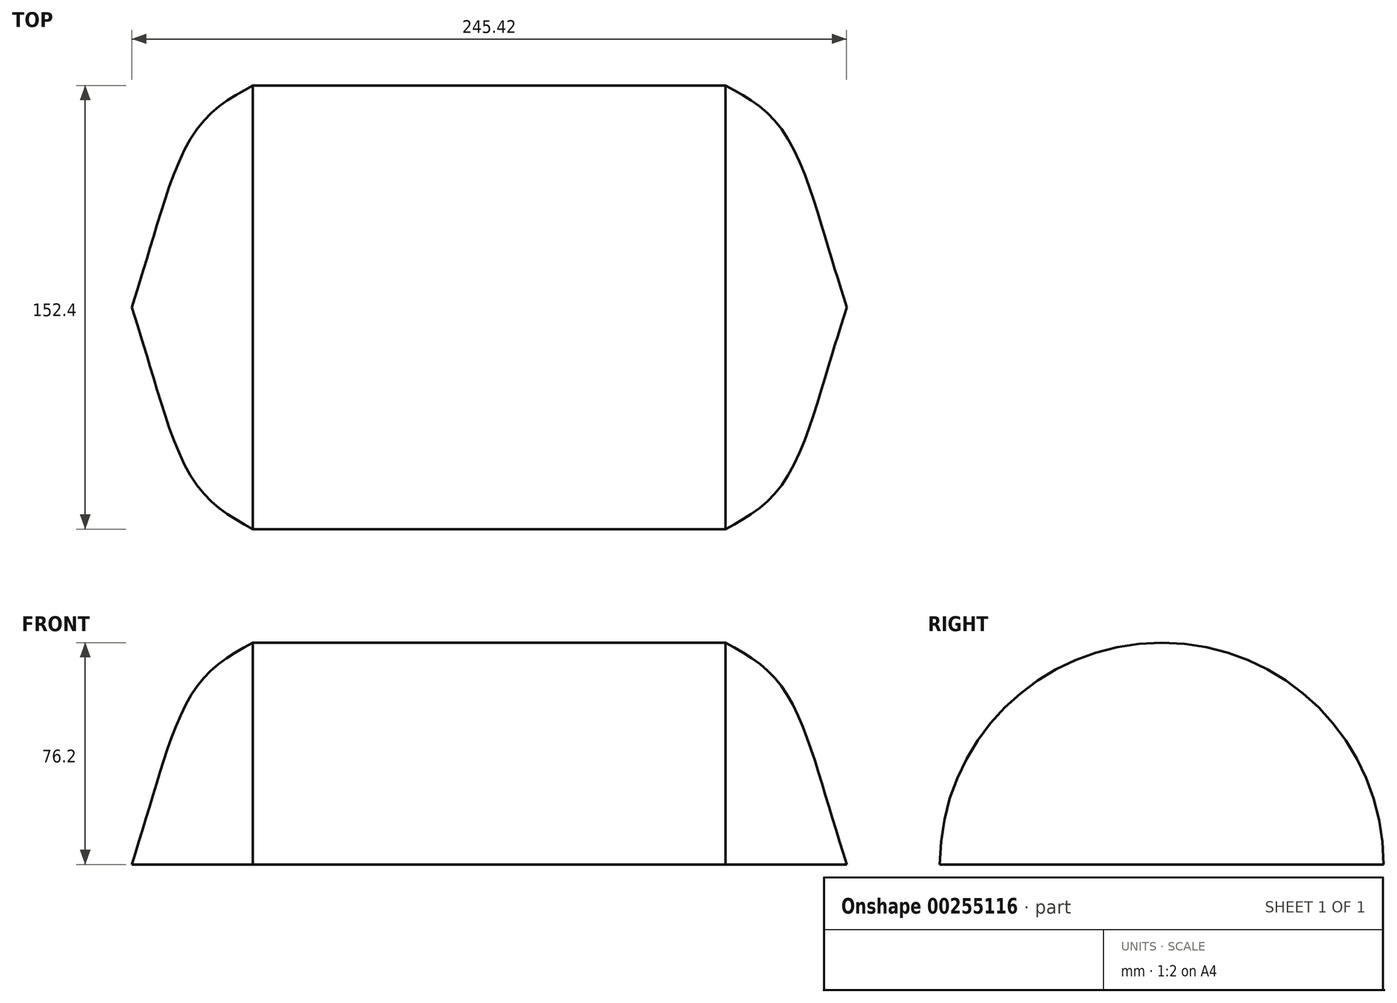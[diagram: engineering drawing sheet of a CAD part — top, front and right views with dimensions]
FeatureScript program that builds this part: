
annotation { "Feature Type Name" : "Feature", "Feature Type Description" : "" }
export const myFeature = defineFeature(function(context is Context, id is Id, definition is map)
    precondition{}
    {
        {
            var Q0;
            Q0=qCreatedBy(makeId("Top.planeOp"),FACE);
            var sketch = newSketch(context, id + "F0", { "sketchPlane" : qUnion([Q0])});
            skLineSegment(sketch, "E0", {"start": v(-122.71, 0) * mm, "end": v(131.29, 0) * mm});
            skLineSegment(sketch, "E1.0", {"start": v(-81.16, 76.2) * mm, "end": v(81.16, 76.2) * mm});
            skFitSpline(sketch, "E2", {"points": [v(-122.71, 0) * mm, v(-114.94, 25.4) * mm, v(-100.23, 61.35) * mm, v(-81.16, 76.2) * mm], "startDerivative": vector(22.9, 73.92) * mm, "endDerivative": vector(68.23, 37.65) * mm});
            skFitSpline(sketch, "E3.MirrorCS", {"points": [v(122.71, 0) * mm, v(114.94, 25.4) * mm, v(100.23, 61.35) * mm, v(81.16, 76.2) * mm], "startDerivative": vector(-22.9, 73.92) * mm, "endDerivative": vector(-68.23, 37.65) * mm});
            skSolve(sketch);
        }
        {
            var Q0;
            Q0=sQuery(id+"F0.wireOp",EDGE,"E1.0");
            var Q1;
            Q1=sQuery(id+"F0.wireOp",EDGE,"E2");
            var Q2;
            Q2=sQuery(id+"F0.wireOp",EDGE,"E3.MirrorCS");
            var Q3;
            Q3=sQuery(id+"F0.wireOp",EDGE,"E0");
            revolve(context, id + "F1", {"bodyType" : ToolBodyType.SURFACE, "surfaceEntities" : qUnion([Q0, Q1, Q2]), "axis" : qUnion([Q3]), "revolveType" : RevolveType.ONE_DIRECTION, "angle" : 180 * degree});
        }
    });
